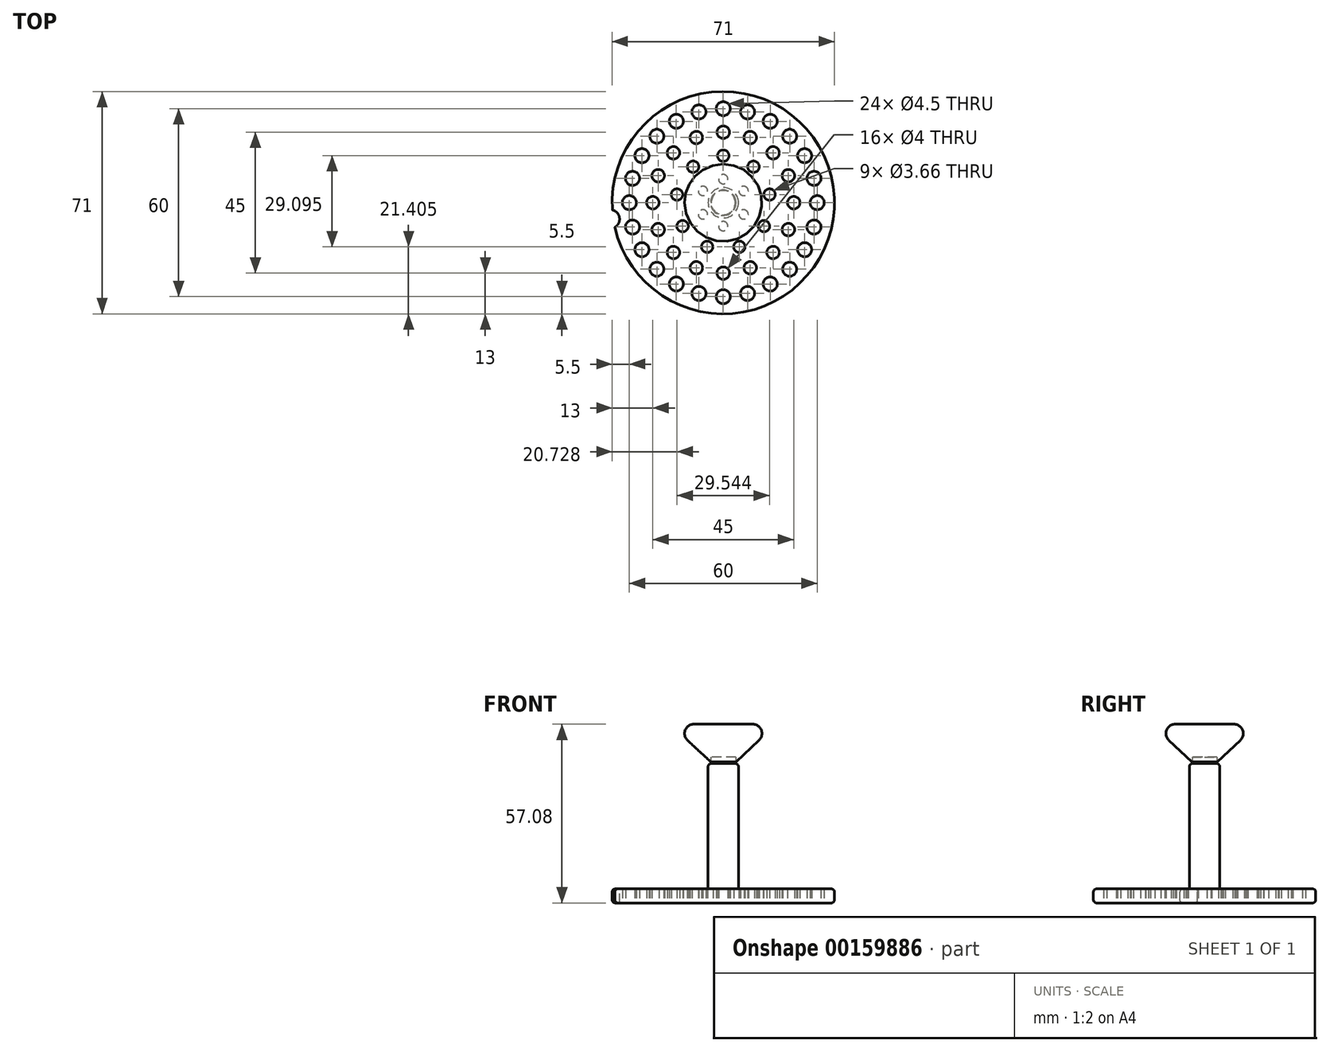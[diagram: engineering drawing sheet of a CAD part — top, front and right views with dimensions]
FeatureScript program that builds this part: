
annotation { "Feature Type Name" : "Feature", "Feature Type Description" : "" }
export const myFeature = defineFeature(function(context is Context, id is Id, definition is map)
    precondition{}
    {
        {
            var Q0;
            Q0=qCreatedBy(makeId("Top.planeOp"),FACE);
            var sketch = newSketch(context, id + "F0", { "sketchPlane" : qUnion([Q0])});
            skCircle(sketch, "E0", {"center": v(0, 0) * mm, "radius": 35.5 * mm});
            skSolve(sketch);
        }
        {
            var Q0;
            Q0=makeQuery(id+"F0.imprint","IMPRINT",FACE,{"disambiguationData":[TD([[makeQuery(id+"F0.imprint","IMPRINT",EDGE,{"derivedFrom":sQuery(id+"F0.wireOp",EDGE,"E0")}),1.0]])]});
            var sketch = newSketch(context, id + "F1", { "sketchPlane" : qUnion([Q0])});
            skCircle(sketch, "E1", {"center": v(0, 0) * mm, "radius": 7.5 * mm, "construction": true});
            skCircle(sketch, "E2", {"center": v(0, 7.5) * mm, "radius": 1.5 * mm});
            skCircle(sketch, "E3.1.1", {"center": v(-6.5, 3.75) * mm, "radius": 1.5 * mm});
            skCircle(sketch, "E3.2.1", {"center": v(-6.5, -3.75) * mm, "radius": 1.5 * mm});
            skCircle(sketch, "E3.3.1", {"center": v(0, -7.5) * mm, "radius": 1.5 * mm});
            skCircle(sketch, "E3.4.1", {"center": v(6.5, -3.75) * mm, "radius": 1.5 * mm});
            skCircle(sketch, "E3.5.1", {"center": v(6.5, 3.75) * mm, "radius": 1.5 * mm});
            skSolve(sketch);
        }
        {
            var Q0;
            Q0=makeQuery(id+"F0.imprint","IMPRINT",FACE,{"disambiguationData":[TD([[makeQuery(id+"F0.imprint","IMPRINT",EDGE,{"derivedFrom":sQuery(id+"F0.wireOp",EDGE,"E0")}),1.0]])]});
            var sketch = newSketch(context, id + "F2", { "sketchPlane" : qUnion([Q0])});
            skCircle(sketch, "E4", {"center": v(0, 0) * mm, "radius": 15 * mm, "construction": true});
            skCircle(sketch, "E5", {"center": v(0, 15) * mm, "radius": 1.83 * mm});
            skCircle(sketch, "E6.1.0", {"center": v(-9.64, 11.5) * mm, "radius": 1.83 * mm});
            skCircle(sketch, "E6.2.0", {"center": v(-14.77, 2.6) * mm, "radius": 1.83 * mm});
            skCircle(sketch, "E6.3.0", {"center": v(-13, -7.5) * mm, "radius": 1.83 * mm});
            skCircle(sketch, "E6.4.0", {"center": v(-5.13, -14.1) * mm, "radius": 1.83 * mm});
            skCircle(sketch, "E6.5.0", {"center": v(5.13, -14.1) * mm, "radius": 1.83 * mm});
            skCircle(sketch, "E6.6.0", {"center": v(13, -7.5) * mm, "radius": 1.83 * mm});
            skCircle(sketch, "E6.7.0", {"center": v(14.77, 2.6) * mm, "radius": 1.83 * mm});
            skCircle(sketch, "E6.8.0", {"center": v(9.64, 11.5) * mm, "radius": 1.83 * mm});
            skSolve(sketch);
        }
        {
            var Q0;
            Q0=makeQuery(id+"F0.imprint","IMPRINT",FACE,{"disambiguationData":[TD([[makeQuery(id+"F0.imprint","IMPRINT",EDGE,{"derivedFrom":sQuery(id+"F0.wireOp",EDGE,"E0")}),1.0]])]});
            var sketch = newSketch(context, id + "F3", { "sketchPlane" : qUnion([Q0])});
            skCircle(sketch, "E7", {"center": v(0, 0) * mm, "radius": 22.5 * mm, "construction": true});
            skCircle(sketch, "E8", {"center": v(0, 22.5) * mm, "radius": 2 * mm});
            skCircle(sketch, "E9.1.0", {"center": v(-8.61, 20.79) * mm, "radius": 2 * mm});
            skCircle(sketch, "E9.2.0", {"center": v(-15.9, 15.9) * mm, "radius": 2 * mm});
            skCircle(sketch, "E9.3.0", {"center": v(-20.79, 8.61) * mm, "radius": 2 * mm});
            skCircle(sketch, "E9.4.0", {"center": v(-22.5, 0) * mm, "radius": 2 * mm});
            skCircle(sketch, "E9.5.0", {"center": v(-20.79, -8.61) * mm, "radius": 2 * mm});
            skCircle(sketch, "E9.6.0", {"center": v(-15.9, -15.9) * mm, "radius": 2 * mm});
            skCircle(sketch, "E9.7.0", {"center": v(-8.61, -20.79) * mm, "radius": 2 * mm});
            skCircle(sketch, "E9.8.0", {"center": v(0, -22.5) * mm, "radius": 2 * mm});
            skCircle(sketch, "E9.9.0", {"center": v(8.61, -20.79) * mm, "radius": 2 * mm});
            skCircle(sketch, "E9.10.0", {"center": v(15.9, -15.9) * mm, "radius": 2 * mm});
            skCircle(sketch, "E9.11.0", {"center": v(20.79, -8.61) * mm, "radius": 2 * mm});
            skCircle(sketch, "E9.12.0", {"center": v(22.5, 0) * mm, "radius": 2 * mm});
            skCircle(sketch, "E9.13.0", {"center": v(20.79, 8.61) * mm, "radius": 2 * mm});
            skCircle(sketch, "E9.14.0", {"center": v(15.9, 15.9) * mm, "radius": 2 * mm});
            skCircle(sketch, "E9.15.0", {"center": v(8.61, 20.79) * mm, "radius": 2 * mm});
            skSolve(sketch);
        }
        {
            var Q0;
            Q0=makeQuery(id+"F0.imprint","IMPRINT",FACE,{"disambiguationData":[TD([[makeQuery(id+"F0.imprint","IMPRINT",EDGE,{"derivedFrom":sQuery(id+"F0.wireOp",EDGE,"E0")}),1.0]])]});
            var sketch = newSketch(context, id + "F4", { "sketchPlane" : qUnion([Q0])});
            skCircle(sketch, "E10", {"center": v(0, 0) * mm, "radius": 30 * mm, "construction": true});
            skCircle(sketch, "E11", {"center": v(0, 30) * mm, "radius": 2.25 * mm});
            skCircle(sketch, "E12.1.0", {"center": v(-7.76, 28.98) * mm, "radius": 2.25 * mm});
            skCircle(sketch, "E12.2.0", {"center": v(-15, 25.98) * mm, "radius": 2.25 * mm});
            skCircle(sketch, "E13.1.3.0", {"center": v(-21.21, 21.21) * mm, "radius": 2.25 * mm});
            skCircle(sketch, "E13.1.4.0", {"center": v(-25.98, 15) * mm, "radius": 2.25 * mm});
            skCircle(sketch, "E13.1.5.0", {"center": v(-28.98, 7.76) * mm, "radius": 2.25 * mm});
            skCircle(sketch, "E13.1.6.0", {"center": v(-30, 0) * mm, "radius": 2.25 * mm});
            skCircle(sketch, "E13.1.7.0", {"center": v(-28.98, -7.76) * mm, "radius": 2.25 * mm});
            skCircle(sketch, "E13.1.8.0", {"center": v(-25.98, -15) * mm, "radius": 2.25 * mm});
            skCircle(sketch, "E13.1.9.0", {"center": v(-21.21, -21.21) * mm, "radius": 2.25 * mm});
            skCircle(sketch, "E13.1.10.0", {"center": v(-15, -25.98) * mm, "radius": 2.25 * mm});
            skCircle(sketch, "E13.1.11.0", {"center": v(-7.76, -28.98) * mm, "radius": 2.25 * mm});
            skCircle(sketch, "E13.1.12.0", {"center": v(0, -30) * mm, "radius": 2.25 * mm});
            skCircle(sketch, "E13.1.13.0", {"center": v(7.76, -28.98) * mm, "radius": 2.25 * mm});
            skCircle(sketch, "E13.1.14.0", {"center": v(15, -25.98) * mm, "radius": 2.25 * mm});
            skCircle(sketch, "E13.1.15.0", {"center": v(21.21, -21.21) * mm, "radius": 2.25 * mm});
            skCircle(sketch, "E13.1.16.0", {"center": v(25.98, -15) * mm, "radius": 2.25 * mm});
            skCircle(sketch, "E13.1.17.0", {"center": v(28.98, -7.76) * mm, "radius": 2.25 * mm});
            skCircle(sketch, "E13.1.18.0", {"center": v(30, 0) * mm, "radius": 2.25 * mm});
            skCircle(sketch, "E13.1.19.0", {"center": v(28.98, 7.76) * mm, "radius": 2.25 * mm});
            skCircle(sketch, "E13.1.20.0", {"center": v(25.98, 15) * mm, "radius": 2.25 * mm});
            skCircle(sketch, "E13.1.21.0", {"center": v(21.21, 21.21) * mm, "radius": 2.25 * mm});
            skCircle(sketch, "E13.1.22.0", {"center": v(15, 25.98) * mm, "radius": 2.25 * mm});
            skCircle(sketch, "E13.1.23.0", {"center": v(7.76, 28.98) * mm, "radius": 2.25 * mm});
            skSolve(sketch);
        }
        {
            var Q0;
            Q0=qSketchRegion(id+"F4",true);
            extrude(context, id + "F5", {"entities" : qUnion([Q0]), "depth" : 5 * mm});
        }
        {
            var Q0;
            Q0=qSketchRegion(id+"F3",true);
            extrude(context, id + "F6", {"entities" : qUnion([Q0]), "depth" : 5 * mm});
        }
        {
            var Q0;
            Q0=qSketchRegion(id+"F2",true);
            extrude(context, id + "F7", {"entities" : qUnion([Q0]), "depth" : 5 * mm});
        }
        {
            var Q0;
            Q0=qSketchRegion(id+"F1",true);
            extrude(context, id + "F8", {"entities" : qUnion([Q0]), "depth" : 5 * mm});
        }
        {
            var Q0;
            Q0=qSketchRegion(id+"F0",true);
            extrude(context, id + "F9", {"entities" : qUnion([Q0]), "depth" : 4.5 * mm});
        }
        {
            var Q0;
            Q0=makeQuery(id+"F5.opExtrude","SWEPT_BODY",BODY,{"disambiguationData":[OSD([sQuery(id+"F4.wireOp",EDGE,"E11")])]});
            var Q1;
            Q1=makeQuery(id+"F5.opExtrude","SWEPT_BODY",BODY,{"disambiguationData":[OSD([sQuery(id+"F4.wireOp",EDGE,"E13.1.3.0")])]});
            var Q2;
            Q2=makeQuery(id+"F5.opExtrude","SWEPT_BODY",BODY,{"disambiguationData":[OSD([sQuery(id+"F4.wireOp",EDGE,"E13.1.7.0")])]});
            var Q3;
            Q3=makeQuery(id+"F5.opExtrude","SWEPT_BODY",BODY,{"disambiguationData":[OSD([sQuery(id+"F4.wireOp",EDGE,"E12.1.0")])]});
            var Q4;
            Q4=makeQuery(id+"F5.opExtrude","SWEPT_BODY",BODY,{"disambiguationData":[OSD([sQuery(id+"F4.wireOp",EDGE,"E12.2.0")])]});
            var Q5;
            Q5=makeQuery(id+"F5.opExtrude","SWEPT_BODY",BODY,{"disambiguationData":[OSD([sQuery(id+"F4.wireOp",EDGE,"E13.1.4.0")])]});
            var Q6;
            Q6=makeQuery(id+"F5.opExtrude","SWEPT_BODY",BODY,{"disambiguationData":[OSD([sQuery(id+"F4.wireOp",EDGE,"E13.1.5.0")])]});
            var Q7;
            Q7=makeQuery(id+"F5.opExtrude","SWEPT_BODY",BODY,{"disambiguationData":[OSD([sQuery(id+"F4.wireOp",EDGE,"E13.1.6.0")])]});
            var Q8;
            Q8=makeQuery(id+"F5.opExtrude","SWEPT_BODY",BODY,{"disambiguationData":[OSD([sQuery(id+"F4.wireOp",EDGE,"E13.1.8.0")])]});
            var Q9;
            Q9=makeQuery(id+"F5.opExtrude","SWEPT_BODY",BODY,{"disambiguationData":[OSD([sQuery(id+"F4.wireOp",EDGE,"E13.1.9.0")])]});
            var Q10;
            Q10=makeQuery(id+"F5.opExtrude","SWEPT_BODY",BODY,{"disambiguationData":[OSD([sQuery(id+"F4.wireOp",EDGE,"E13.1.10.0")])]});
            var Q11;
            Q11=makeQuery(id+"F5.opExtrude","SWEPT_BODY",BODY,{"disambiguationData":[OSD([sQuery(id+"F4.wireOp",EDGE,"E13.1.11.0")])]});
            var Q12;
            Q12=makeQuery(id+"F5.opExtrude","SWEPT_BODY",BODY,{"disambiguationData":[OSD([sQuery(id+"F4.wireOp",EDGE,"E13.1.12.0")])]});
            var Q13;
            Q13=makeQuery(id+"F5.opExtrude","SWEPT_BODY",BODY,{"disambiguationData":[OSD([sQuery(id+"F4.wireOp",EDGE,"E13.1.13.0")])]});
            var Q14;
            Q14=makeQuery(id+"F5.opExtrude","SWEPT_BODY",BODY,{"disambiguationData":[OSD([sQuery(id+"F4.wireOp",EDGE,"E13.1.14.0")])]});
            var Q15;
            Q15=makeQuery(id+"F5.opExtrude","SWEPT_BODY",BODY,{"disambiguationData":[OSD([sQuery(id+"F4.wireOp",EDGE,"E13.1.15.0")])]});
            var Q16;
            Q16=makeQuery(id+"F5.opExtrude","SWEPT_BODY",BODY,{"disambiguationData":[OSD([sQuery(id+"F4.wireOp",EDGE,"E13.1.16.0")])]});
            var Q17;
            Q17=makeQuery(id+"F5.opExtrude","SWEPT_BODY",BODY,{"disambiguationData":[OSD([sQuery(id+"F4.wireOp",EDGE,"E13.1.17.0")])]});
            var Q18;
            Q18=makeQuery(id+"F5.opExtrude","SWEPT_BODY",BODY,{"disambiguationData":[OSD([sQuery(id+"F4.wireOp",EDGE,"E13.1.18.0")])]});
            var Q19;
            Q19=makeQuery(id+"F5.opExtrude","SWEPT_BODY",BODY,{"disambiguationData":[OSD([sQuery(id+"F4.wireOp",EDGE,"E13.1.19.0")])]});
            var Q20;
            Q20=makeQuery(id+"F5.opExtrude","SWEPT_BODY",BODY,{"disambiguationData":[OSD([sQuery(id+"F4.wireOp",EDGE,"E13.1.20.0")])]});
            var Q21;
            Q21=makeQuery(id+"F5.opExtrude","SWEPT_BODY",BODY,{"disambiguationData":[OSD([sQuery(id+"F4.wireOp",EDGE,"E13.1.21.0")])]});
            var Q22;
            Q22=makeQuery(id+"F5.opExtrude","SWEPT_BODY",BODY,{"disambiguationData":[OSD([sQuery(id+"F4.wireOp",EDGE,"E13.1.22.0")])]});
            var Q23;
            Q23=makeQuery(id+"F5.opExtrude","SWEPT_BODY",BODY,{"disambiguationData":[OSD([sQuery(id+"F4.wireOp",EDGE,"E13.1.23.0")])]});
            var Q24;
            Q24=makeQuery(id+"F6.opExtrude","SWEPT_BODY",BODY,{"disambiguationData":[OSD([sQuery(id+"F3.wireOp",EDGE,"E9.15.0")])]});
            var Q25;
            Q25=makeQuery(id+"F6.opExtrude","SWEPT_BODY",BODY,{"disambiguationData":[OSD([sQuery(id+"F3.wireOp",EDGE,"E8")])]});
            var Q26;
            Q26=makeQuery(id+"F6.opExtrude","SWEPT_BODY",BODY,{"disambiguationData":[OSD([sQuery(id+"F3.wireOp",EDGE,"E9.1.0")])]});
            var Q27;
            Q27=makeQuery(id+"F6.opExtrude","SWEPT_BODY",BODY,{"disambiguationData":[OSD([sQuery(id+"F3.wireOp",EDGE,"E9.2.0")])]});
            var Q28;
            Q28=makeQuery(id+"F6.opExtrude","SWEPT_BODY",BODY,{"disambiguationData":[OSD([sQuery(id+"F3.wireOp",EDGE,"E9.3.0")])]});
            var Q29;
            Q29=makeQuery(id+"F6.opExtrude","SWEPT_BODY",BODY,{"disambiguationData":[OSD([sQuery(id+"F3.wireOp",EDGE,"E9.4.0")])]});
            var Q30;
            Q30=makeQuery(id+"F6.opExtrude","SWEPT_BODY",BODY,{"disambiguationData":[OSD([sQuery(id+"F3.wireOp",EDGE,"E9.5.0")])]});
            var Q31;
            Q31=makeQuery(id+"F6.opExtrude","SWEPT_BODY",BODY,{"disambiguationData":[OSD([sQuery(id+"F3.wireOp",EDGE,"E9.6.0")])]});
            var Q32;
            Q32=makeQuery(id+"F6.opExtrude","SWEPT_BODY",BODY,{"disambiguationData":[OSD([sQuery(id+"F3.wireOp",EDGE,"E9.7.0")])]});
            var Q33;
            Q33=makeQuery(id+"F6.opExtrude","SWEPT_BODY",BODY,{"disambiguationData":[OSD([sQuery(id+"F3.wireOp",EDGE,"E9.8.0")])]});
            var Q34;
            Q34=makeQuery(id+"F6.opExtrude","SWEPT_BODY",BODY,{"disambiguationData":[OSD([sQuery(id+"F3.wireOp",EDGE,"E9.9.0")])]});
            var Q35;
            Q35=makeQuery(id+"F6.opExtrude","SWEPT_BODY",BODY,{"disambiguationData":[OSD([sQuery(id+"F3.wireOp",EDGE,"E9.10.0")])]});
            var Q36;
            Q36=makeQuery(id+"F6.opExtrude","SWEPT_BODY",BODY,{"disambiguationData":[OSD([sQuery(id+"F3.wireOp",EDGE,"E9.11.0")])]});
            var Q37;
            Q37=makeQuery(id+"F6.opExtrude","SWEPT_BODY",BODY,{"disambiguationData":[OSD([sQuery(id+"F3.wireOp",EDGE,"E9.12.0")])]});
            var Q38;
            Q38=makeQuery(id+"F6.opExtrude","SWEPT_BODY",BODY,{"disambiguationData":[OSD([sQuery(id+"F3.wireOp",EDGE,"E9.13.0")])]});
            var Q39;
            Q39=makeQuery(id+"F6.opExtrude","SWEPT_BODY",BODY,{"disambiguationData":[OSD([sQuery(id+"F3.wireOp",EDGE,"E9.14.0")])]});
            var Q40;
            Q40=makeQuery(id+"F7.opExtrude","SWEPT_BODY",BODY,{"disambiguationData":[OSD([sQuery(id+"F2.wireOp",EDGE,"E6.8.0")])]});
            var Q41;
            Q41=makeQuery(id+"F7.opExtrude","SWEPT_BODY",BODY,{"disambiguationData":[OSD([sQuery(id+"F2.wireOp",EDGE,"E6.7.0")])]});
            var Q42;
            Q42=makeQuery(id+"F7.opExtrude","SWEPT_BODY",BODY,{"disambiguationData":[OSD([sQuery(id+"F2.wireOp",EDGE,"E6.6.0")])]});
            var Q43;
            Q43=makeQuery(id+"F7.opExtrude","SWEPT_BODY",BODY,{"disambiguationData":[OSD([sQuery(id+"F2.wireOp",EDGE,"E6.5.0")])]});
            var Q44;
            Q44=makeQuery(id+"F7.opExtrude","SWEPT_BODY",BODY,{"disambiguationData":[OSD([sQuery(id+"F2.wireOp",EDGE,"E6.4.0")])]});
            var Q45;
            Q45=makeQuery(id+"F7.opExtrude","SWEPT_BODY",BODY,{"disambiguationData":[OSD([sQuery(id+"F2.wireOp",EDGE,"E6.3.0")])]});
            var Q46;
            Q46=makeQuery(id+"F7.opExtrude","SWEPT_BODY",BODY,{"disambiguationData":[OSD([sQuery(id+"F2.wireOp",EDGE,"E6.2.0")])]});
            var Q47;
            Q47=makeQuery(id+"F7.opExtrude","SWEPT_BODY",BODY,{"disambiguationData":[OSD([sQuery(id+"F2.wireOp",EDGE,"E6.1.0")])]});
            var Q48;
            Q48=makeQuery(id+"F7.opExtrude","SWEPT_BODY",BODY,{"disambiguationData":[OSD([sQuery(id+"F2.wireOp",EDGE,"E5")])]});
            var Q49;
            Q49=makeQuery(id+"F8.opExtrude","SWEPT_BODY",BODY,{"disambiguationData":[OSD([sQuery(id+"F1.wireOp",EDGE,"E2")])]});
            var Q50;
            Q50=makeQuery(id+"F8.opExtrude","SWEPT_BODY",BODY,{"disambiguationData":[OSD([sQuery(id+"F1.wireOp",EDGE,"E3.5.1")])]});
            var Q51;
            Q51=makeQuery(id+"F8.opExtrude","SWEPT_BODY",BODY,{"disambiguationData":[OSD([sQuery(id+"F1.wireOp",EDGE,"E3.4.1")])]});
            var Q52;
            Q52=makeQuery(id+"F8.opExtrude","SWEPT_BODY",BODY,{"disambiguationData":[OSD([sQuery(id+"F1.wireOp",EDGE,"E3.3.1")])]});
            var Q53;
            Q53=makeQuery(id+"F8.opExtrude","SWEPT_BODY",BODY,{"disambiguationData":[OSD([sQuery(id+"F1.wireOp",EDGE,"E3.2.1")])]});
            var Q54;
            Q54=makeQuery(id+"F8.opExtrude","SWEPT_BODY",BODY,{"disambiguationData":[OSD([sQuery(id+"F1.wireOp",EDGE,"E3.1.1")])]});
            var Q55;
            Q55=makeQuery(id+"F9.opExtrude","SWEPT_BODY",BODY,{"disambiguationData":[OSD([sQuery(id+"F0.wireOp",EDGE,"E0")])]});
            booleanBodies(context, id + "F10", {"operationType" : BooleanOperationType.SUBTRACTION, "tools" : qUnion([Q0, Q1, Q2, Q3, Q4, Q5, Q6, Q7, Q8, Q9, Q10, Q11, Q12, Q13, Q14, Q15, Q16, Q17, Q18, Q19, Q20, Q21, Q22, Q23, Q24, Q25, Q26, Q27, Q28, Q29, Q30, Q31, Q32, Q33, Q34, Q35, Q36, Q37, Q38, Q39, Q40, Q41, Q42, Q43, Q44, Q45, Q46, Q47, Q48, Q49, Q50, Q51, Q52, Q53, Q54]), "targets" : qUnion([Q55])});
        }
        {
            var Q0;
            Q0=makeQuery(id+"F9.opExtrude","CAP_EDGE",EDGE,{"disambiguationData":[OSD([sQuery(id+"F0.wireOp",EDGE,"E0")])],"isStart":true});
            var Q1;
            Q1=makeQuery(id+"F9.opExtrude","CAP_EDGE",EDGE,{"disambiguationData":[OSD([sQuery(id+"F0.wireOp",EDGE,"E0")])],"isStart":false});
            fillet(context, id + "F11", {"entities" : qUnion([Q0, Q1]), "radius" : 1 * mm, "tangentPropagation" : true, "allowEdgeOverflow" : false});
        }
        {
            var Q0;
            Q0=makeQuery(id+"F9.opExtrude","CAP_FACE",FACE,{"disambiguationData":[OSD([sQuery(id+"F0.wireOp",EDGE,"E0")])],"isStart":false});
            var sketch = newSketch(context, id + "F12", { "sketchPlane" : qUnion([Q0])});
            skCircle(sketch, "E14", {"center": v(0, 0) * mm, "radius": 4.85 * mm});
            skSolve(sketch);
        }
        {
            var Q0;
            Q0=makeQuery(id+"F12.imprint","IMPRINT",FACE,{"disambiguationData":[TD([[makeQuery(id+"F12.imprint","IMPRINT",EDGE,{"derivedFrom":sQuery(id+"F12.wireOp",EDGE,"E14")}),1.0]])]});
            extrude(context, id + "F13", {"entities" : qUnion([Q0]), "operationType" : NewBodyOperationType.ADD, "depth" : 40 * mm, "offsetDistance" : 25 * mm});
        }
        {
            var Q0;
            Q0=makeQuery(id+"F13.opExtrude","CAP_EDGE",EDGE,{"disambiguationData":[OSD([sQuery(id+"F12.wireOp",EDGE,"E14")])],"isStart":false});
            fillet(context, id + "F14", {"entities" : qUnion([Q0]), "radius" : 1 * mm, "tangentPropagation" : true, "allowEdgeOverflow" : false});
        }
        {
            var Q0;
            Q0=makeQuery(id+"F9.opExtrude","CAP_FACE",FACE,{"disambiguationData":[OSD([sQuery(id+"F0.wireOp",EDGE,"E0")])],"isStart":false});
            var sketch = newSketch(context, id + "F15", { "sketchPlane" : qUnion([Q0])});
            skCircle(sketch, "E15", {"center": v(0, 0) * mm, "radius": 36.5 * mm, "construction": true});
            skCircle(sketch, "E16", {"center": v(-36.12, -5.23) * mm, "radius": 3 * mm});
            skSolve(sketch);
        }
        {
            var Q0;
            Q0=makeQuery(id+"F15.imprint","IMPRINT",FACE,{"disambiguationData":[TD([[makeQuery(id+"F15.imprint","IMPRINT",EDGE,{"derivedFrom":sQuery(id+"F15.wireOp",EDGE,"E16")}),1.0]])]});
            extrude(context, id + "F16", {"entities" : qUnion([Q0]), "operationType" : NewBodyOperationType.REMOVE, "oppositeDirection" : true, "depth" : 25 * mm});
        }
        {
            var Q0;
            Q0=makeQuery(id+"F13.opExtrude","CAP_FACE",FACE,{"disambiguationData":[OSD([sQuery(id+"F12.wireOp",EDGE,"E14")])],"isStart":false});
            var sketch = newSketch(context, id + "F17", { "sketchPlane" : qUnion([Q0])});
            skCircle(sketch, "E17", {"center": v(0, 0) * mm, "radius": 3.98 * mm});
            skSolve(sketch);
        }
        {
            var Q0;
            Q0=qSketchRegion(id+"F17",true);
            extrude(context, id + "F18", {"entities" : qUnion([Q0]), "operationType" : NewBodyOperationType.ADD, "depth" : 2 * mm, "offsetDistance" : 25 * mm});
        }
        {
            var Q0;
            Q0=qCreatedBy(makeId("Front.planeOp"),FACE);
            var sketch = newSketch(context, id + "F19", { "sketchPlane" : qUnion([Q0])});
            skLineSegment(sketch, "E18", {"start": v(0, 64.6) * mm, "end": v(0, 85.08) * mm, "construction": true});
            skLineSegment(sketch, "E19", {"start": v(0, 85.08) * mm, "end": v(-17, 85.08) * mm});
            skLineSegment(sketch, "E20", {"start": v(-17, 85.08) * mm, "end": v(-4.06, 73.08) * mm});
            skLineSegment(sketch, "E21", {"start": v(-4.06, 73.08) * mm, "end": v(0, 73.08) * mm});
            skLineSegment(sketch, "E22", {"start": v(0, 73.08) * mm, "end": v(0, 85.08) * mm});
            skSolve(sketch);
        }
        {
            var Q0;
            Q0=makeQuery(id+"F19.imprint","IMPRINT",FACE,{"disambiguationData":[TD([[makeQuery(id+"F19.imprint","IMPRINT",EDGE,{"derivedFrom":sQuery(id+"F19.wireOp",EDGE,"E19")}),1.0]])]});
            var Q1;
            Q1=sQuery(id+"F19.wireOp",EDGE,"E22");
            revolve(context, id + "F20", {"operationType" : NewBodyOperationType.ADD, "surfaceOperationType" : NewSurfaceOperationType.NEW, "entities" : qUnion([Q0]), "axis" : qUnion([Q1]), "revolveType" : RevolveType.FULL});
        }
        {
            var Q0;
            Q0=makeQuery(id+"F20.opRevolve","SWEPT_EDGE",EDGE,{"disambiguationData":[OSD([sQuery(id+"F19.wireOp",EDGE,"E19"),sQuery(id+"F19.wireOp",EDGE,"E20")])]});
            fillet(context, id + "F21", {"entities" : qUnion([Q0]), "radius" : 3 * mm, "tangentPropagation" : true, "allowEdgeOverflow" : false});
        }
        {
            var Q0;
            Q0=makeQuery(id+"F20.opRevolve","SWEPT_BODY",BODY,{"disambiguationData":[OSD([sQuery(id+"F19.wireOp",EDGE,"E19"),sQuery(id+"F19.wireOp",EDGE,"E20"),sQuery(id+"F19.wireOp",EDGE,"E21"),sQuery(id+"F19.wireOp",EDGE,"E22")])]});
            transform(context, id + "F22", {"entities" : qUnion([Q0]), "transformType" : TransformType.TRANSLATION_3D, "dx" : 0 * mm, "dy" : 0 * mm, "dz" : -28 * mm, "makeCopy" : false});
        }
        {
            var Q0;
            Q0=makeQuery(id+"F20.opRevolve","SWEPT_BODY",BODY,{"disambiguationData":[OSD([sQuery(id+"F19.wireOp",EDGE,"E19"),sQuery(id+"F19.wireOp",EDGE,"E20"),sQuery(id+"F19.wireOp",EDGE,"E21"),sQuery(id+"F19.wireOp",EDGE,"E22")])]});
            transform(context, id + "F23", {"entities" : qUnion([Q0]), "transformType" : TransformType.TRANSLATION_3D, "dx" : 0 * mm, "dy" : 0 * mm, "dz" : 0 * mm, "makeCopy" : true});
        }
        {
            var Q0;
            Q0=makeQuery(id+"F23.opPattern","COPY",BODY,{"derivedFrom":makeQuery(id+"F20.opRevolve","SWEPT_BODY",BODY,{"disambiguationData":[OSD([sQuery(id+"F19.wireOp",EDGE,"E19"),sQuery(id+"F19.wireOp",EDGE,"E20"),sQuery(id+"F19.wireOp",EDGE,"E21"),sQuery(id+"F19.wireOp",EDGE,"E22")])]}),"instanceName":"1"});
            deleteBodies(context, id + "F24", {"entities" : qUnion([Q0])});
        }
    });
